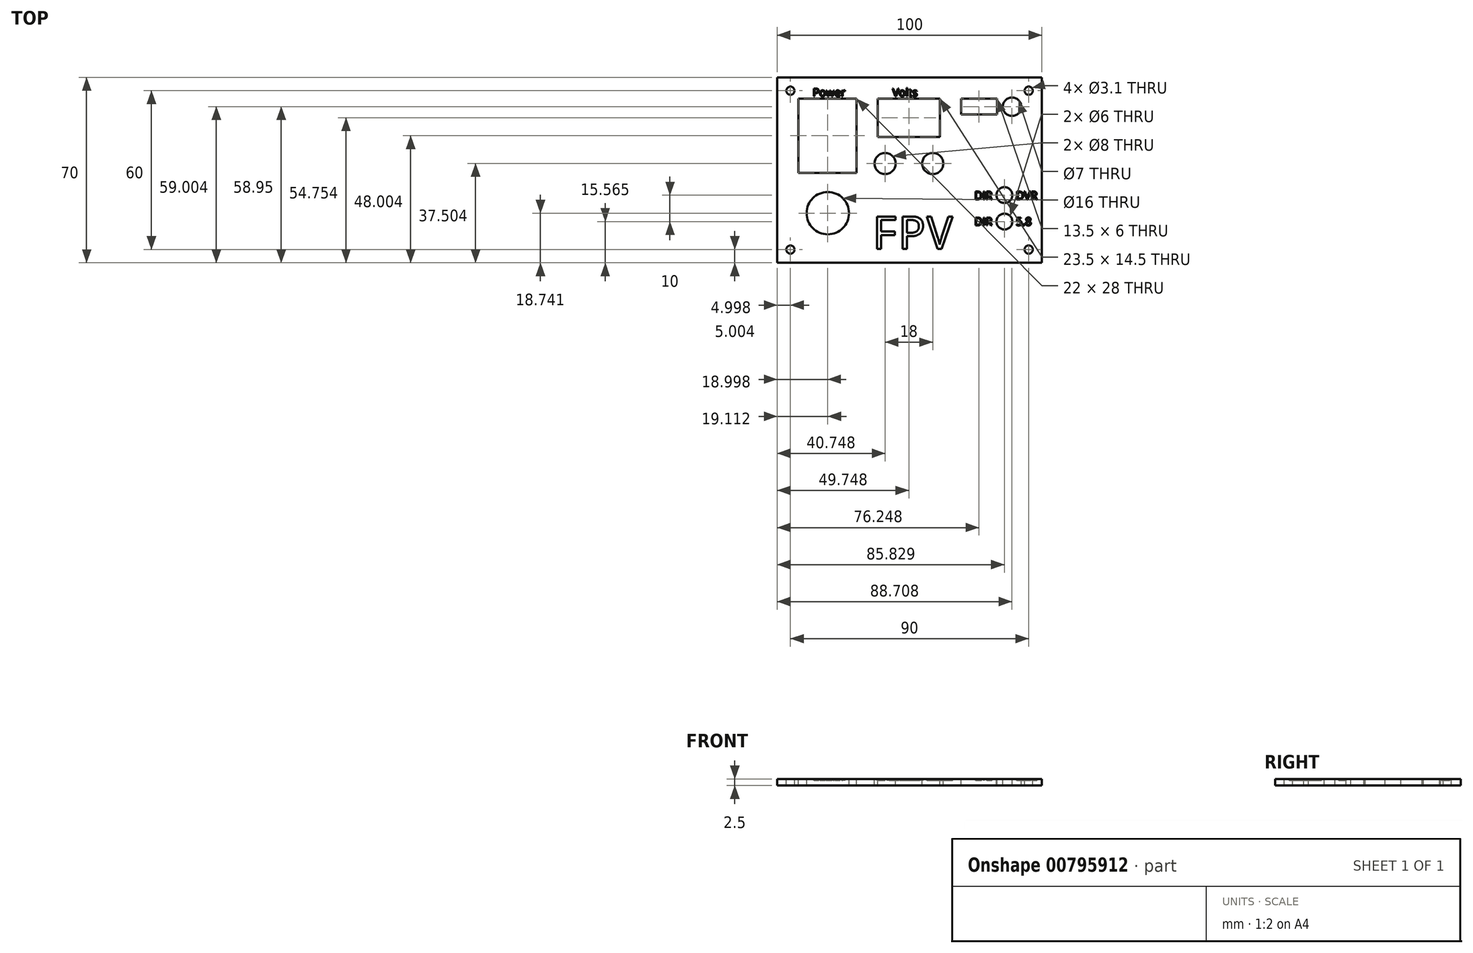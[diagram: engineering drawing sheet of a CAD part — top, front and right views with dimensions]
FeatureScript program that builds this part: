
annotation { "Feature Type Name" : "Feature", "Feature Type Description" : "" }
export const myFeature = defineFeature(function(context is Context, id is Id, definition is map)
    precondition{}
    {
        {
            var Q0;
            Q0=qCreatedBy(makeId("Top.planeOp"),FACE);
            var sketch = newSketch(context, id + "F0", { "sketchPlane" : qUnion([Q0])});
            skLineSegment(sketch, "E0.bottom", {"start": v(-58.3, 39.35) * mm, "end": v(41.7, 39.35) * mm});
            skLineSegment(sketch, "E0.top", {"start": v(-58.3, -30.65) * mm, "end": v(41.7, -30.65) * mm});
            skLineSegment(sketch, "E0.left", {"start": v(-58.3, 39.35) * mm, "end": v(-58.3, -30.65) * mm});
            skLineSegment(sketch, "E0.right", {"start": v(41.7, 39.35) * mm, "end": v(41.7, -30.65) * mm});
            skSolve(sketch);
        }
        {
            var Q0;
            Q0=makeQuery(id+"F0.imprint","IMPRINT",FACE,{"disambiguationData":[TD([[makeQuery(id+"F0.imprint","IMPRINT",EDGE,{"derivedFrom":sQuery(id+"F0.wireOp",EDGE,"E0.bottom")}),-1.0]])]});
            extrude(context, id + "F1", {"entities" : qUnion([Q0]), "depth" : 2.5 * mm, "offsetDistance" : 25 * mm});
        }
        {
            var Q0;
            Q0=makeQuery(id+"F1.opExtrude","CAP_FACE",FACE,{"disambiguationData":[OSD([sQuery(id+"F0.wireOp",EDGE,"E0.bottom"),sQuery(id+"F0.wireOp",EDGE,"E0.top"),sQuery(id+"F0.wireOp",EDGE,"E0.left"),sQuery(id+"F0.wireOp",EDGE,"E0.right")])],"isStart":false});
            var sketch = newSketch(context, id + "F2", { "sketchPlane" : qUnion([Q0])});
            skLineSegment(sketch, "E1", {"start": v(-58.3, 39.35) * mm, "end": v(-50.3, 39.35) * mm, "construction": true});
            skLineSegment(sketch, "E2", {"start": v(-50.3, 39.35) * mm, "end": v(-50.3, 31.35) * mm, "construction": true});
            skLineSegment(sketch, "E3", {"start": v(-50.3, 31.35) * mm, "end": v(-28.3, 31.35) * mm});
            skLineSegment(sketch, "E4", {"start": v(-28.3, 31.35) * mm, "end": v(-28.3, 3.35) * mm});
            skLineSegment(sketch, "E5", {"start": v(-28.3, 3.35) * mm, "end": v(-50.3, 3.35) * mm});
            skLineSegment(sketch, "E6", {"start": v(-50.3, 3.35) * mm, "end": v(-50.3, 31.35) * mm});
            skSolve(sketch);
        }
        {
            var Q0;
            Q0 = qSketchRegion(id + "F2", true);
            extrude(context, id + "F3", {"entities" : qUnion([Q0]), "operationType" : NewBodyOperationType.REMOVE, "oppositeDirection" : true, "depth" : 3 * mm, "offsetDistance" : 25 * mm});
        }
        {
            var Q0;
            Q0=makeQuery(id+"F1.opExtrude","CAP_FACE",FACE,{"disambiguationData":[OSD([sQuery(id+"F0.wireOp",EDGE,"E0.bottom"),sQuery(id+"F0.wireOp",EDGE,"E0.top"),sQuery(id+"F0.wireOp",EDGE,"E0.left"),sQuery(id+"F0.wireOp",EDGE,"E0.right")])],"isStart":false});
            var sketch = newSketch(context, id + "F4", { "sketchPlane" : qUnion([Q0])});
            skLineSegment(sketch, "E7", {"start": v(-28.3, 31.35) * mm, "end": v(-20.3, 31.35) * mm, "construction": true});
            skLineSegment(sketch, "E8", {"start": v(-20.3, 31.35) * mm, "end": v(-20.3, 16.85) * mm});
            skLineSegment(sketch, "E9", {"start": v(-20.3, 16.85) * mm, "end": v(3.2, 16.85) * mm});
            skLineSegment(sketch, "E10", {"start": v(3.2, 16.85) * mm, "end": v(3.2, 31.35) * mm});
            skLineSegment(sketch, "E11", {"start": v(3.2, 31.35) * mm, "end": v(-20.3, 31.35) * mm});
            skSolve(sketch);
        }
        {
            var Q0;
            Q0=makeQuery(id+"F4.imprint","IMPRINT",FACE,{"disambiguationData":[TD([[makeQuery(id+"F4.imprint","IMPRINT",EDGE,{"derivedFrom":sQuery(id+"F4.wireOp",EDGE,"E8")}),1.0]])]});
            extrude(context, id + "F5", {"entities" : qUnion([Q0]), "operationType" : NewBodyOperationType.REMOVE, "oppositeDirection" : true, "depth" : 3 * mm, "offsetDistance" : 25 * mm});
        }
        {
            var Q0;
            Q0=makeQuery(id+"F1.opExtrude","CAP_FACE",FACE,{"disambiguationData":[OSD([sQuery(id+"F0.wireOp",EDGE,"E0.bottom"),sQuery(id+"F0.wireOp",EDGE,"E0.top"),sQuery(id+"F0.wireOp",EDGE,"E0.left"),sQuery(id+"F0.wireOp",EDGE,"E0.right")])],"isStart":false});
            var sketch = newSketch(context, id + "F6", { "sketchPlane" : qUnion([Q0])});
            skLineSegment(sketch, "E12", {"start": v(3.2, 31.35) * mm, "end": v(11.2, 31.35) * mm, "construction": true});
            skLineSegment(sketch, "E13", {"start": v(11.2, 31.35) * mm, "end": v(11.2, 25.35) * mm});
            skLineSegment(sketch, "E14", {"start": v(11.2, 25.35) * mm, "end": v(24.7, 25.35) * mm});
            skLineSegment(sketch, "E15", {"start": v(24.7, 25.35) * mm, "end": v(24.7, 31.35) * mm});
            skLineSegment(sketch, "E16", {"start": v(24.7, 31.35) * mm, "end": v(11.2, 31.35) * mm});
            skSolve(sketch);
        }
        {
            var Q0;
            Q0=makeQuery(id+"F6.imprint","IMPRINT",FACE,{"disambiguationData":[TD([[makeQuery(id+"F6.imprint","IMPRINT",EDGE,{"derivedFrom":sQuery(id+"F6.wireOp",EDGE,"E13")}),1.0]])]});
            extrude(context, id + "F7", {"entities" : qUnion([Q0]), "operationType" : NewBodyOperationType.REMOVE, "oppositeDirection" : true, "depth" : 3 * mm, "offsetDistance" : 25 * mm});
        }
        {
            var Q0;
            Q0=makeQuery(id+"F1.opExtrude","CAP_FACE",FACE,{"disambiguationData":[OSD([sQuery(id+"F0.wireOp",EDGE,"E0.bottom"),sQuery(id+"F0.wireOp",EDGE,"E0.top"),sQuery(id+"F0.wireOp",EDGE,"E0.left"),sQuery(id+"F0.wireOp",EDGE,"E0.right")])],"isStart":false});
            var sketch = newSketch(context, id + "F8", { "sketchPlane" : qUnion([Q0])});
            skLineSegment(sketch, "E17", {"start": v(24.7, 31.35) * mm, "end": v(28.7, 31.35) * mm, "construction": true});
            skCircle(sketch, "E18", {"center": v(30.4, 28.3) * mm, "radius": 3.5 * mm});
            skPoint(sketch, "E18.second.point", {"position": v(33.67, 27.04) * mm});
            skPoint(sketch, "E18.third.point", {"position": v(28.7, 25.25) * mm});
            skSolve(sketch);
        }
        {
            var Q0;
            Q0=makeQuery(id+"F8.imprint","IMPRINT",FACE,{"disambiguationData":[TD([[makeQuery(id+"F8.imprint","IMPRINT",EDGE,{"derivedFrom":sQuery(id+"F8.wireOp",EDGE,"E18")}),1.0]])]});
            extrude(context, id + "F9", {"entities" : qUnion([Q0]), "operationType" : NewBodyOperationType.REMOVE, "oppositeDirection" : true, "depth" : 3 * mm, "offsetDistance" : 25 * mm});
        }
        {
            var Q0;
            Q0=makeQuery(id+"F1.opExtrude","CAP_FACE",FACE,{"disambiguationData":[OSD([sQuery(id+"F0.wireOp",EDGE,"E0.bottom"),sQuery(id+"F0.wireOp",EDGE,"E0.top"),sQuery(id+"F0.wireOp",EDGE,"E0.left"),sQuery(id+"F0.wireOp",EDGE,"E0.right")])],"isStart":false});
            var sketch = newSketch(context, id + "F10", { "sketchPlane" : qUnion([Q0])});
            skText(sketch, "E19", { "text": "Power", "fontName": "OpenSans-Regular.ttf"});
            skText(sketch, "E20", { "text": "Volts", "fontName": "OpenSans-Regular.ttf"});
            skText(sketch, "E21", { "text": "FPV", "fontName": "DroidSansMono.ttf"});
            const initialGuessF10  = {"E19": [-0.0449, 0.03223, 1, 0, 0.003], "E20": [-0.0148, 0.03223, 1, 0, 0.003], "E21": [-0.02264, -0.0254, 1, 0, 0.01234]};
            skSetInitialGuess(sketch, initialGuessF10);
            skSolve(sketch);
        }
        {
            var Q0;
            Q0 = qSketchRegion(id + "F10", true);
            extrude(context, id + "F11", {"entities" : qUnion([Q0]), "operationType" : NewBodyOperationType.REMOVE, "oppositeDirection" : true, "depth" : 0.5 * mm, "offsetDistance" : 25 * mm});
        }
        {
            var Q0;
            {var subQ0=sQuery(id+"F0.wireOp",EDGE,"E0.right");var subQ1=sQuery(id+"F0.wireOp",EDGE,"E0.bottom");var subQ2=sQuery(id+"F0.wireOp",EDGE,"E0.left");var subQ3=sQuery(id+"F0.wireOp",EDGE,"E0.top");Q0=makeQuery(id+"F11.boolean.opBoolean","SPLIT",FACE,{"disambiguationData":[TD([makeQuery(id+"F1.opExtrude","SWEPT_FACE",FACE,{"disambiguationData":[OSD([subQ1])]})])],"derivedFrom":makeQuery(id+"F1.opExtrude","CAP_FACE",FACE,{"disambiguationData":[OSD([subQ1,subQ3,subQ2,subQ0])],"isStart":false})});}
            var sketch = newSketch(context, id + "F12", { "sketchPlane" : qUnion([Q0])});
            skLineSegment(sketch, "E22", {"start": v(-58.3, 39.35) * mm, "end": v(-53.3, 39.35) * mm, "construction": true});
            skLineSegment(sketch, "E23", {"start": v(-53.3, 39.35) * mm, "end": v(-53.3, 34.35) * mm, "construction": true});
            skLineSegment(sketch, "E24", {"start": v(-53.3, 34.35) * mm, "end": v(-58.3, 34.35) * mm, "construction": true});
            skLineSegment(sketch, "E25", {"start": v(-58.3, 34.35) * mm, "end": v(-58.3, 39.35) * mm, "construction": true});
            skCircle(sketch, "E26", {"center": v(-53.3, 34.35) * mm, "radius": 1.55 * mm});
            skLineSegment(sketch, "E27", {"start": v(-58.3, -30.65) * mm, "end": v(-53.3, -30.65) * mm, "construction": true});
            skLineSegment(sketch, "E28", {"start": v(-53.3, -30.65) * mm, "end": v(-53.3, -25.65) * mm, "construction": true});
            skCircle(sketch, "E29", {"center": v(-53.3, -25.65) * mm, "radius": 1.55 * mm});
            skLineSegment(sketch, "E30", {"start": v(41.7, -30.65) * mm, "end": v(36.7, -30.65) * mm, "construction": true});
            skLineSegment(sketch, "E31", {"start": v(36.7, -30.65) * mm, "end": v(36.7, -25.65) * mm, "construction": true});
            skLineSegment(sketch, "E32", {"start": v(41.7, 39.35) * mm, "end": v(36.7, 39.35) * mm, "construction": true});
            skLineSegment(sketch, "E33", {"start": v(36.7, 39.35) * mm, "end": v(36.7, 34.35) * mm, "construction": true});
            skCircle(sketch, "E34", {"center": v(36.7, 34.35) * mm, "radius": 1.55 * mm});
            skCircle(sketch, "E35", {"center": v(36.7, -25.65) * mm, "radius": 1.55 * mm});
            skSolve(sketch);
        }
        {
            var Q0;
            Q0=makeQuery(id+"F12.imprint","IMPRINT",FACE,{"disambiguationData":[TD([[makeQuery(id+"F12.imprint","IMPRINT",EDGE,{"derivedFrom":sQuery(id+"F12.wireOp",EDGE,"E34")}),1.0]])]});
            var Q1;
            Q1=makeQuery(id+"F12.imprint","IMPRINT",FACE,{"disambiguationData":[TD([[makeQuery(id+"F12.imprint","IMPRINT",EDGE,{"derivedFrom":sQuery(id+"F12.wireOp",EDGE,"E26")}),1.0]])]});
            var Q2;
            Q2=makeQuery(id+"F12.imprint","IMPRINT",FACE,{"disambiguationData":[TD([[makeQuery(id+"F12.imprint","IMPRINT",EDGE,{"derivedFrom":sQuery(id+"F12.wireOp",EDGE,"E35")}),1.0]])]});
            var Q3;
            Q3=makeQuery(id+"F12.imprint","IMPRINT",FACE,{"disambiguationData":[TD([[makeQuery(id+"F12.imprint","IMPRINT",EDGE,{"derivedFrom":sQuery(id+"F12.wireOp",EDGE,"E29")}),1.0]])]});
            extrude(context, id + "F13", {"entities" : qUnion([Q0, Q1, Q2, Q3]), "operationType" : NewBodyOperationType.REMOVE, "oppositeDirection" : true, "depth" : 3 * mm, "offsetDistance" : 25 * mm});
        }
        {
            var Q0;
            {var subQ0=sQuery(id+"F0.wireOp",EDGE,"E0.right");var subQ1=sQuery(id+"F0.wireOp",EDGE,"E0.bottom");var subQ2=sQuery(id+"F0.wireOp",EDGE,"E0.left");var subQ3=sQuery(id+"F0.wireOp",EDGE,"E0.top");Q0=makeQuery(id+"F11.boolean.opBoolean","SPLIT",FACE,{"disambiguationData":[TD([makeQuery(id+"F1.opExtrude","SWEPT_FACE",FACE,{"disambiguationData":[OSD([subQ1])]})])],"derivedFrom":makeQuery(id+"F1.opExtrude","CAP_FACE",FACE,{"disambiguationData":[OSD([subQ1,subQ3,subQ2,subQ0])],"isStart":false})});}
            var sketch = newSketch(context, id + "F14", { "sketchPlane" : qUnion([Q0])});
            skCircle(sketch, "E36", {"center": v(27.53, -5.09) * mm, "radius": 3 * mm});
            skLineSegment(sketch, "E37", {"start": v(27.53, -5.09) * mm, "end": v(27.53, -15.09) * mm, "construction": true});
            skCircle(sketch, "E38", {"center": v(27.53, -15.09) * mm, "radius": 3 * mm});
            skSolve(sketch);
        }
        {
            var Q0;
            Q0=makeQuery(id+"F14.imprint","IMPRINT",FACE,{"disambiguationData":[TD([[makeQuery(id+"F14.imprint","IMPRINT",EDGE,{"derivedFrom":sQuery(id+"F14.wireOp",EDGE,"E36")}),1.0]])]});
            var Q1;
            Q1=makeQuery(id+"F14.imprint","IMPRINT",FACE,{"disambiguationData":[TD([[makeQuery(id+"F14.imprint","IMPRINT",EDGE,{"derivedFrom":sQuery(id+"F14.wireOp",EDGE,"E38")}),1.0]])]});
            extrude(context, id + "F15", {"entities" : qUnion([Q0, Q1]), "operationType" : NewBodyOperationType.REMOVE, "oppositeDirection" : true, "depth" : 3 * mm, "offsetDistance" : 25 * mm});
        }
        {
            var Q0;
            {var subQ0=sQuery(id+"F0.wireOp",EDGE,"E0.right");var subQ1=sQuery(id+"F0.wireOp",EDGE,"E0.bottom");var subQ2=sQuery(id+"F0.wireOp",EDGE,"E0.left");var subQ3=sQuery(id+"F0.wireOp",EDGE,"E0.top");Q0=makeQuery(id+"F11.boolean.opBoolean","SPLIT",FACE,{"disambiguationData":[TD([makeQuery(id+"F1.opExtrude","SWEPT_FACE",FACE,{"disambiguationData":[OSD([subQ1])]})])],"derivedFrom":makeQuery(id+"F1.opExtrude","CAP_FACE",FACE,{"disambiguationData":[OSD([subQ1,subQ3,subQ2,subQ0])],"isStart":false})});}
            var sketch = newSketch(context, id + "F16", { "sketchPlane" : qUnion([Q0])});
            skText(sketch, "E39", { "text": "DVR", "fontName": "OpenSans-Regular.ttf"});
            skText(sketch, "E40", { "text": "DIR", "fontName": "OpenSans-Regular.ttf"});
            skText(sketch, "E41", { "text": "5.8", "fontName": "OpenSans-Regular.ttf"});
            skText(sketch, "E42", { "text": "DIR", "fontName": "OpenSans-Regular.ttf"});
            skLineSegment(sketch, "E43", {"start": v(23.14, -3.7) * mm, "end": v(31.9, -3.7) * mm, "construction": true});
            skLineSegment(sketch, "E44", {"start": v(31.9, -13.55) * mm, "end": v(23.14, -13.55) * mm, "construction": true});
            skLineSegment(sketch, "E45", {"start": v(23.14, -6.7) * mm, "end": v(23.14, -13.55) * mm, "construction": true});
            skLineSegment(sketch, "E46", {"start": v(31.9, -13.55) * mm, "end": v(31.9, -6.7) * mm, "construction": true});
            const initialGuessF16  = {"E39": [0.0319, -0.0067, 1, 0, 0.003], "E40": [0.01617, -0.0067, 1, 0, 0.003], "E41": [0.0319, -0.01655, 1, 0, 0.003], "E42": [0.01617, -0.01655, 1, 0, 0.003]};
            skSetInitialGuess(sketch, initialGuessF16);
            skSolve(sketch);
        }
        {
            var Q0;
            Q0 = qSketchRegion(id + "F16", true);
            extrude(context, id + "F17", {"entities" : qUnion([Q0]), "operationType" : NewBodyOperationType.REMOVE, "oppositeDirection" : true, "depth" : 0.5 * mm, "offsetDistance" : 25 * mm});
        }
        {
            var Q0;
            {var subQ106=sQuery(id+"F0.wireOp",EDGE,"E0.bottom");var subQ107=makeQuery(id+"F1.opExtrude","SWEPT_FACE",FACE,{"disambiguationData":[OSD([subQ106])]});var subQ108=sQuery(id+"F0.wireOp",EDGE,"E0.left");var subQ112=sQuery(id+"F0.wireOp",EDGE,"E0.top");var subQ116=sQuery(id+"F0.wireOp",EDGE,"E0.right");Q0=makeQuery(id+"F17.boolean.opBoolean","SPLIT",FACE,{"disambiguationData":[TD([subQ107])],"derivedFrom":makeQuery(id+"F11.boolean.opBoolean","SPLIT",FACE,{"disambiguationData":[TD([subQ107])],"derivedFrom":makeQuery(id+"F1.opExtrude","CAP_FACE",FACE,{"disambiguationData":[OSD([subQ106,subQ112,subQ108,subQ116])],"isStart":false})})});}
            var sketch = newSketch(context, id + "F18", { "sketchPlane" : qUnion([Q0])});
            skLineSegment(sketch, "E47", {"start": v(-8.55, 16.85) * mm, "end": v(-8.55, 6.85) * mm, "construction": true});
            skLineSegment(sketch, "E48", {"start": v(-8.55, 6.85) * mm, "end": v(0.45, 6.85) * mm, "construction": true});
            skLineSegment(sketch, "E49", {"start": v(-8.55, 6.85) * mm, "end": v(-17.55, 6.85) * mm, "construction": true});
            skCircle(sketch, "E50", {"center": v(-17.55, 6.85) * mm, "radius": 4 * mm});
            skCircle(sketch, "E51", {"center": v(0.45, 6.85) * mm, "radius": 4 * mm});
            skSolve(sketch);
        }
        {
            var Q0;
            Q0=makeQuery(id+"F18.imprint","IMPRINT",FACE,{"disambiguationData":[TD([[makeQuery(id+"F18.imprint","IMPRINT",EDGE,{"derivedFrom":sQuery(id+"F18.wireOp",EDGE,"E50")}),1.0]])]});
            var Q1;
            Q1=makeQuery(id+"F18.imprint","IMPRINT",FACE,{"disambiguationData":[TD([[makeQuery(id+"F18.imprint","IMPRINT",EDGE,{"derivedFrom":sQuery(id+"F18.wireOp",EDGE,"E51")}),1.0]])]});
            extrude(context, id + "F19", {"entities" : qUnion([Q0, Q1]), "operationType" : NewBodyOperationType.REMOVE, "oppositeDirection" : true, "depth" : 3 * mm, "offsetDistance" : 25 * mm});
        }
        {
            var Q0;
            {var subQ106=sQuery(id+"F0.wireOp",EDGE,"E0.bottom");var subQ107=makeQuery(id+"F1.opExtrude","SWEPT_FACE",FACE,{"disambiguationData":[OSD([subQ106])]});var subQ108=sQuery(id+"F0.wireOp",EDGE,"E0.left");var subQ112=sQuery(id+"F0.wireOp",EDGE,"E0.top");var subQ116=sQuery(id+"F0.wireOp",EDGE,"E0.right");Q0=makeQuery(id+"F17.boolean.opBoolean","SPLIT",FACE,{"disambiguationData":[TD([subQ107])],"derivedFrom":makeQuery(id+"F11.boolean.opBoolean","SPLIT",FACE,{"disambiguationData":[TD([subQ107])],"derivedFrom":makeQuery(id+"F1.opExtrude","CAP_FACE",FACE,{"disambiguationData":[OSD([subQ106,subQ112,subQ108,subQ116])],"isStart":false})})});}
            var sketch = newSketch(context, id + "F20", { "sketchPlane" : qUnion([Q0])});
            skCircle(sketch, "E52", {"center": v(-39.19, -11.9) * mm, "radius": 8 * mm});
            skSolve(sketch);
        }
        {
            var Q0;
            Q0=makeQuery(id+"F20.imprint","IMPRINT",FACE,{"disambiguationData":[TD([[makeQuery(id+"F20.imprint","IMPRINT",EDGE,{"derivedFrom":sQuery(id+"F20.wireOp",EDGE,"E52")}),1.0]])]});
            extrude(context, id + "F21", {"entities" : qUnion([Q0]), "operationType" : NewBodyOperationType.REMOVE, "oppositeDirection" : true, "depth" : 3 * mm, "offsetDistance" : 25 * mm});
        }
    });
